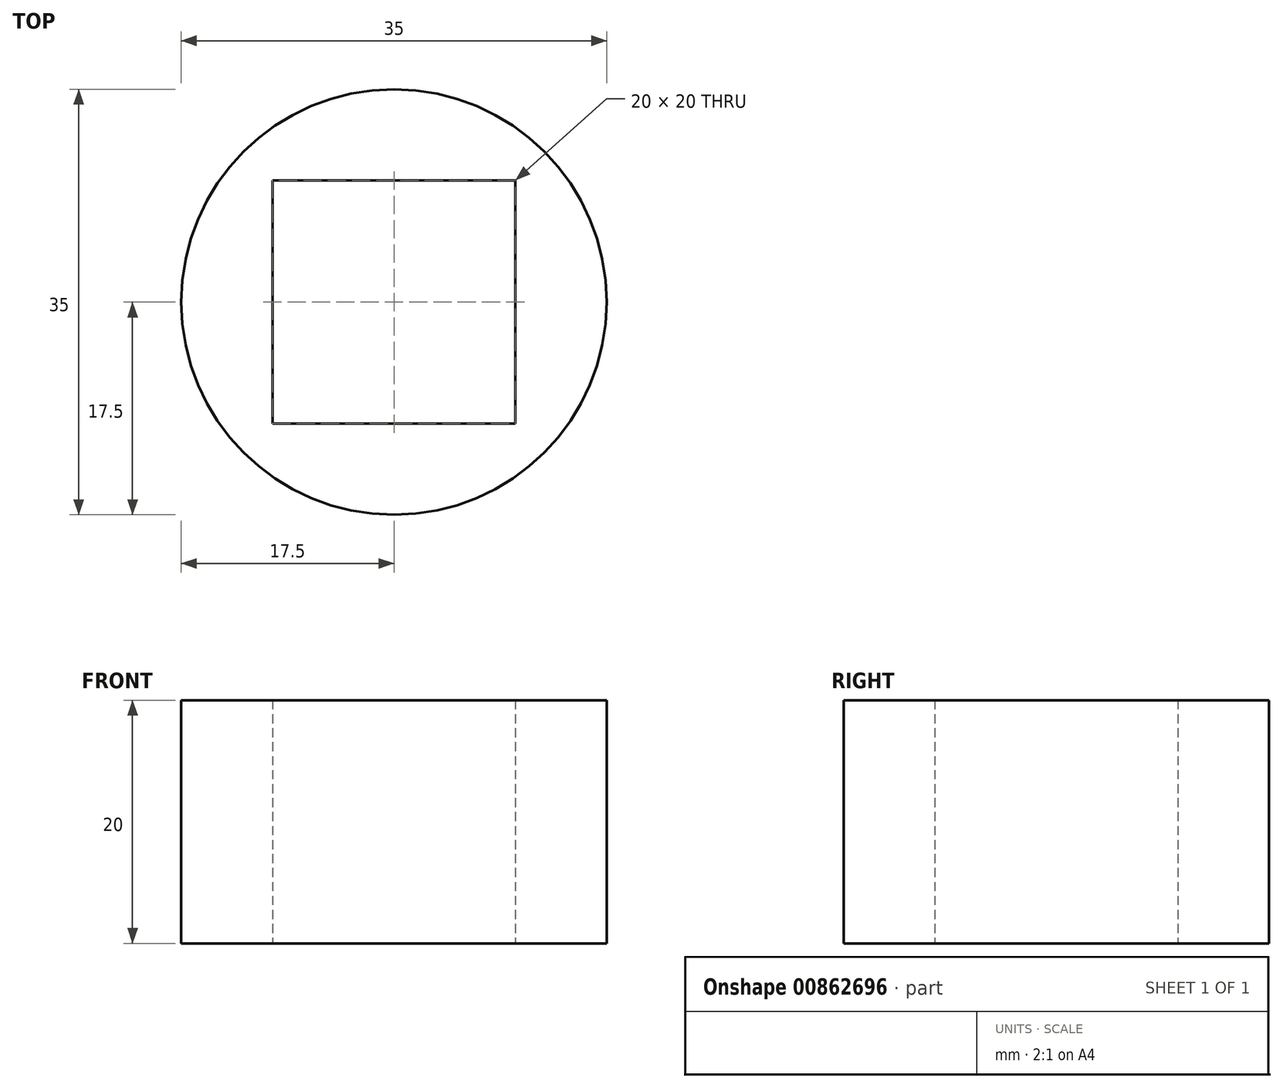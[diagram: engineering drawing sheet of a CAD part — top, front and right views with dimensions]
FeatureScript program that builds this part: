
annotation { "Feature Type Name" : "Feature", "Feature Type Description" : "" }
export const myFeature = defineFeature(function(context is Context, id is Id, definition is map)
    precondition{}
    {
        {
            var Q0;
            Q0=qCreatedBy(makeId("Top.planeOp"),FACE);
            var sketch = newSketch(context, id + "F0", { "sketchPlane" : qUnion([Q0])});
            skCircle(sketch, "E0", {"center": v(0, 0) * mm, "radius": 17.5 * mm});
            skLineSegment(sketch, "E1.bottom", {"start": v(10, 10) * mm, "end": v(-10, 10) * mm});
            skLineSegment(sketch, "E1.top", {"start": v(10, -10) * mm, "end": v(-10, -10) * mm});
            skLineSegment(sketch, "E1.left", {"start": v(10, 10) * mm, "end": v(10, -10) * mm});
            skLineSegment(sketch, "E1.right", {"start": v(-10, 10) * mm, "end": v(-10, -10) * mm});
            skSolve(sketch);
        }
        {
            var Q0;
            Q0=makeQuery(id+"F0.imprint","IMPRINT",FACE,{"disambiguationData":[TD([[makeQuery(id+"F0.imprint","IMPRINT",EDGE,{"derivedFrom":sQuery(id+"F0.wireOp",EDGE,"E0")}),1.0]])]});
            extrude(context, id + "F1", {"entities" : qUnion([Q0]), "depth" : 20 * mm, "offsetDistance" : 25 * mm});
        }
    });
